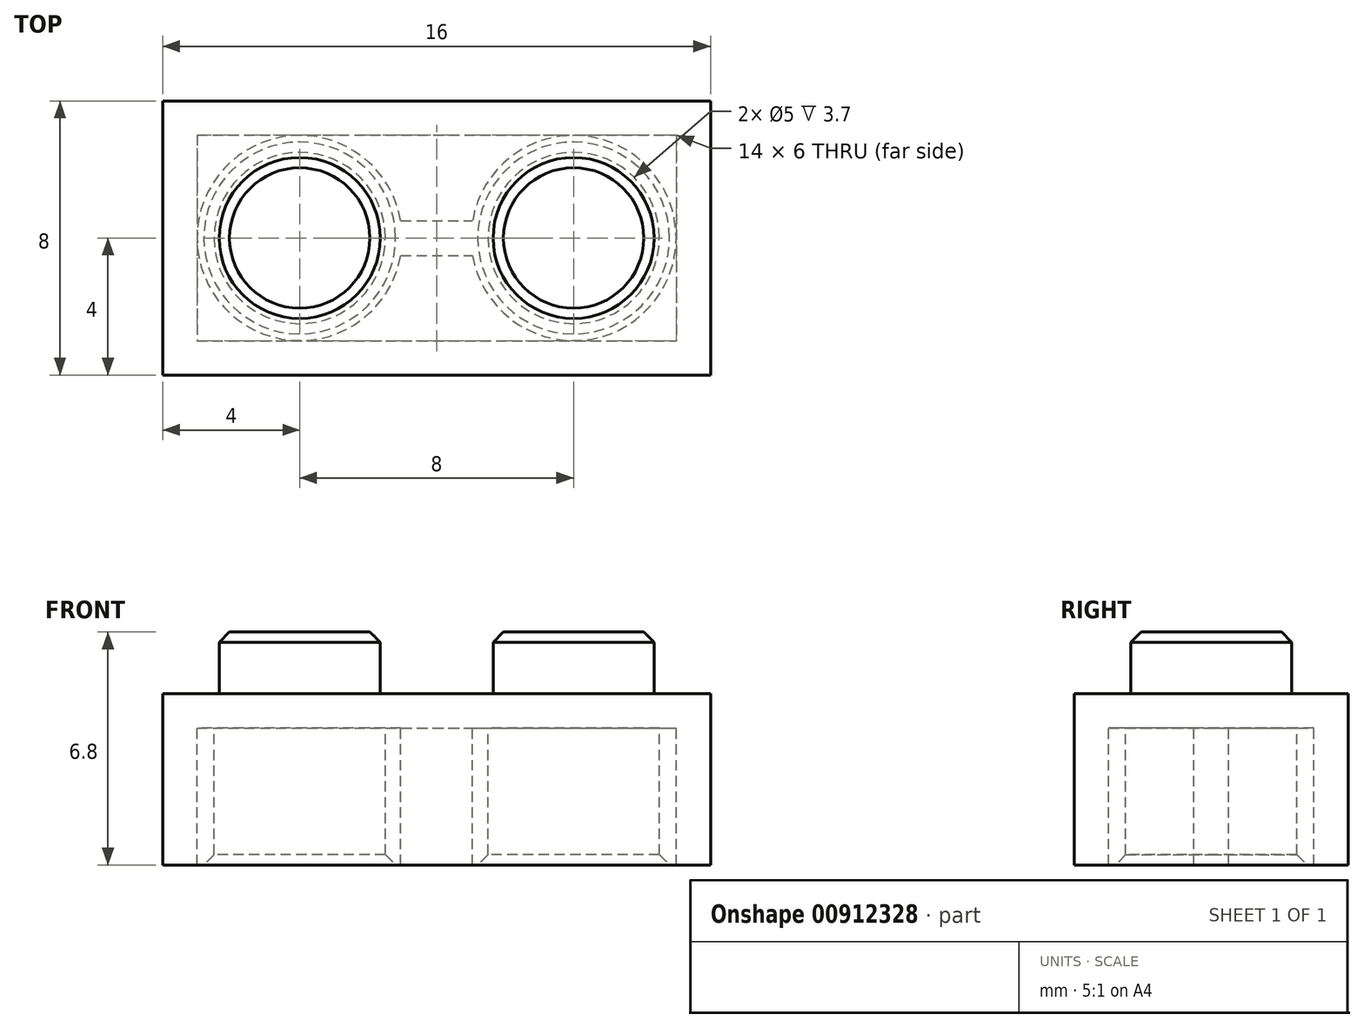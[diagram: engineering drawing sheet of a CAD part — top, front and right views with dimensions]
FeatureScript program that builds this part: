
annotation { "Feature Type Name" : "Feature", "Feature Type Description" : "" }
export const myFeature = defineFeature(function(context is Context, id is Id, definition is map)
    precondition{}
    {
        {
            var Q0;
            Q0=qCreatedBy(makeId("Top.planeOp"),FACE);
            var sketch = newSketch(context, id + "F0", { "sketchPlane" : qUnion([Q0])});
            skLineSegment(sketch, "E0.bottom", {"start": v(-8, 4) * mm, "end": v(8, 4) * mm});
            skLineSegment(sketch, "E0.top", {"start": v(-8, -4) * mm, "end": v(8, -4) * mm});
            skLineSegment(sketch, "E0.left", {"start": v(-8, 4) * mm, "end": v(-8, -4) * mm});
            skLineSegment(sketch, "E0.right", {"start": v(8, 4) * mm, "end": v(8, -4) * mm});
            skCircle(sketch, "E1", {"center": v(-4, 0) * mm, "radius": 2.5 * mm});
            skCircle(sketch, "E2", {"center": v(-4, 0) * mm, "radius": 2.35 * mm});
            skCircle(sketch, "E3", {"center": v(-4, 0) * mm, "radius": 3 * mm});
            skCircle(sketch, "E4.1.0.0", {"center": v(4, 0) * mm, "radius": 3 * mm});
            skCircle(sketch, "E4.1.0.1", {"center": v(4, 0) * mm, "radius": 2.5 * mm});
            skCircle(sketch, "E4.1.0.2", {"center": v(4, 0) * mm, "radius": 2.35 * mm});
            skLineSegment(sketch, "E4.direction1", {"start": v(-4, 0) * mm, "end": v(4, 0) * mm, "construction": true});
            skLineSegment(sketch, "E5.0", {"start": v(-7, 3) * mm, "end": v(7, 3) * mm});
            skLineSegment(sketch, "E5.1", {"start": v(-7, 3) * mm, "end": v(-7, -3) * mm});
            skLineSegment(sketch, "E6.0", {"start": v(-7, -3) * mm, "end": v(7, -3) * mm});
            skLineSegment(sketch, "E6.1", {"start": v(7, 3) * mm, "end": v(7, -3) * mm});
            skLineSegment(sketch, "E7.trimOffspring", {"start": v(-1.05, 0.5) * mm, "end": v(1.05, 0.5) * mm});
            skLineSegment(sketch, "E8.trimOffspring", {"start": v(-1.05, -0.5) * mm, "end": v(1.05, -0.5) * mm});
            skSolve(sketch);
        }
        {
            var Q0;
            Q0 = qSketchRegion(id + "F0", true);
            var Q1;
            Q1=makeQuery(id+"F0.imprint","IMPRINT",FACE,{"disambiguationData":[TD([[makeQuery(id+"F0.imprint","IMPRINT",EDGE,{"derivedFrom":sQuery(id+"F0.wireOp",EDGE,"E3")}),-1.0]])]});
            var Q2;
            Q2=makeQuery(id+"F0.imprint","IMPRINT",FACE,{"disambiguationData":[TD([[makeQuery(id+"F0.imprint","IMPRINT",EDGE,{"derivedFrom":sQuery(id+"F0.wireOp",EDGE,"E1")}),1.0]])]});
            var Q3;
            Q3=makeQuery(id+"F0.imprint","IMPRINT",FACE,{"disambiguationData":[TD([[makeQuery(id+"F0.imprint","IMPRINT",EDGE,{"derivedFrom":sQuery(id+"F0.wireOp",EDGE,"E1")}),-1.0]])]});
            var Q4;
            Q4=makeQuery(id+"F0.imprint","IMPRINT",FACE,{"disambiguationData":[TD([[makeQuery(id+"F0.imprint","IMPRINT",EDGE,{"derivedFrom":sQuery(id+"F0.wireOp",EDGE,"E4.1.0.1")}),1.0]])]});
            var Q5;
            Q5=makeQuery(id+"F0.imprint","IMPRINT",FACE,{"disambiguationData":[TD([[makeQuery(id+"F0.imprint","IMPRINT",EDGE,{"derivedFrom":sQuery(id+"F0.wireOp",EDGE,"E4.1.0.0")}),1.0]])]});
            var Q6;
            Q6=makeQuery(id+"F0.imprint","IMPRINT",FACE,{"disambiguationData":[TD([[makeQuery(id+"F0.imprint","IMPRINT",EDGE,{"derivedFrom":sQuery(id+"F0.wireOp",EDGE,"E4.1.0.2")}),1.0]])]});
            var Q7;
            Q7=makeQuery(id+"F0.imprint","IMPRINT",FACE,{"disambiguationData":[TD([[makeQuery(id+"F0.imprint","IMPRINT",EDGE,{"derivedFrom":sQuery(id+"F0.wireOp",EDGE,"E2")}),1.0]])]});
            var Q8;
            Q8=makeQuery(id+"F0.imprint","IMPRINT",FACE,{"disambiguationData":[TD([[makeQuery(id+"F0.imprint","IMPRINT",EDGE,{"derivedFrom":sQuery(id+"F0.wireOp",EDGE,"E5.0")}),-1.0]])]});
            var Q9;
            {var subQ0=sQuery(id+"F0.wireOp",EDGE,"E7.trimOffspring");Q9=makeQuery(id+"F0.imprint","IMPRINT",FACE,{"disambiguationData":[TD([[makeQuery(id+"F0.imprint","IMPRINT",EDGE,{"derivedFrom":subQ0}),1.0]])]});}
            var Q10;
            {var subQ0=sQuery(id+"F0.wireOp",EDGE,"E8.trimOffspring");Q10=makeQuery(id+"F0.imprint","IMPRINT",FACE,{"disambiguationData":[TD([[makeQuery(id+"F0.imprint","IMPRINT",EDGE,{"derivedFrom":subQ0}),-1.0]])]});}
            var Q11;
            {var subQ0=sQuery(id+"F0.wireOp",EDGE,"E6.1");var subQ1=sQuery(id+"F0.wireOp",EDGE,"E4.1.0.0");var subQ2=makeQuery(id+"F0.imprint","INTERSECT",VERTEX,{"derivedFrom":[subQ1,subQ0]});Q11=makeQuery(id+"F0.imprint","IMPRINT",FACE,{"disambiguationData":[TD([[makeQuery(id+"F0.imprint","IMPRINT",EDGE,{"disambiguationData":[TD([[subQ2,1.0]])],"derivedFrom":subQ1}),-1.0]])]});}
            var Q12;
            {var subQ0=sQuery(id+"F0.wireOp",EDGE,"E7.trimOffspring");Q12=makeQuery(id+"F0.imprint","IMPRINT",FACE,{"disambiguationData":[TD([[makeQuery(id+"F0.imprint","IMPRINT",EDGE,{"derivedFrom":subQ0}),-1.0]])]});}
            extrude(context, id + "F1", {"entities" : qUnion([Q0, Q1, Q2, Q3, Q4, Q5, Q6, Q7, Q8, Q9, Q10, Q11, Q12]), "oppositeDirection" : true, "depth" : 1 * mm, "offsetDistance" : 25 * mm});
        }
        {
            var Q0;
            Q0=makeQuery(id+"F0.imprint","IMPRINT",FACE,{"disambiguationData":[TD([[makeQuery(id+"F0.imprint","IMPRINT",EDGE,{"derivedFrom":sQuery(id+"F0.wireOp",EDGE,"E2")}),1.0]])]});
            var Q1;
            Q1=makeQuery(id+"F0.imprint","IMPRINT",FACE,{"disambiguationData":[TD([[makeQuery(id+"F0.imprint","IMPRINT",EDGE,{"derivedFrom":sQuery(id+"F0.wireOp",EDGE,"E4.1.0.2")}),1.0]])]});
            extrude(context, id + "F2", {"entities" : qUnion([Q0, Q1]), "operationType" : NewBodyOperationType.ADD, "depth" : 1.8 * mm, "offsetDistance" : 25 * mm});
        }
        {
            var Q0;
            Q0=makeQuery(id+"F0.imprint","IMPRINT",FACE,{"disambiguationData":[TD([[makeQuery(id+"F0.imprint","IMPRINT",EDGE,{"derivedFrom":sQuery(id+"F0.wireOp",EDGE,"E4.1.0.0")}),1.0]])]});
            var Q1;
            Q1=makeQuery(id+"F1.opExtrude","CAP_FACE",FACE,{"disambiguationData":[OSD([sQuery(id+"F0.wireOp",EDGE,"E3"),sQuery(id+"F0.wireOp",EDGE,"E4.1.0.0"),sQuery(id+"F0.wireOp",EDGE,"E7.trimOffspring"),sQuery(id+"F0.wireOp",EDGE,"E8.trimOffspring")])],"isStart":false});
            var Q2;
            {var subQ0=sQuery(id+"F0.wireOp",EDGE,"E7.trimOffspring");Q2=makeQuery(id+"F0.imprint","IMPRINT",FACE,{"disambiguationData":[TD([[makeQuery(id+"F0.imprint","IMPRINT",EDGE,{"derivedFrom":subQ0}),-1.0]])]});}
            var Q3;
            Q3=makeQuery(id+"F0.imprint","IMPRINT",FACE,{"disambiguationData":[TD([[makeQuery(id+"F0.imprint","IMPRINT",EDGE,{"derivedFrom":sQuery(id+"F0.wireOp",EDGE,"E0.bottom")}),-1.0]])]});
            var Q4;
            Q4=makeQuery(id+"F0.imprint","IMPRINT",FACE,{"disambiguationData":[TD([[makeQuery(id+"F0.imprint","IMPRINT",EDGE,{"derivedFrom":sQuery(id+"F0.wireOp",EDGE,"E1")}),-1.0]])]});
            extrude(context, id + "F3", {"entities" : qUnion([Q0, Q1, Q2, Q3, Q4]), "operationType" : NewBodyOperationType.ADD, "oppositeDirection" : true, "depth" : 5 * mm, "offsetDistance" : 25 * mm});
        }
        {
            var Q0;
            Q0=makeQuery(id+"F2.opExtrude","CAP_EDGE",EDGE,{"disambiguationData":[OSD([sQuery(id+"F0.wireOp",EDGE,"E2")])],"isStart":false});
            var Q1;
            Q1=makeQuery(id+"F2.opExtrude","CAP_EDGE",EDGE,{"disambiguationData":[OSD([sQuery(id+"F0.wireOp",EDGE,"E4.1.0.2")])],"isStart":false});
            var Q2;
            Q2=makeQuery(id+"F3.opExtrude","CAP_EDGE",EDGE,{"disambiguationData":[OSD([sQuery(id+"F0.wireOp",EDGE,"E1")])],"isStart":false});
            var Q3;
            Q3=makeQuery(id+"F3.opExtrude","CAP_EDGE",EDGE,{"disambiguationData":[OSD([sQuery(id+"F0.wireOp",EDGE,"E4.1.0.1")])],"isStart":false});
            chamfer(context, id + "F4", {"entities" : qUnion([Q0, Q1, Q2, Q3]), "width" : .3 * mm, "tangentPropagation" : true});
        }
    });
